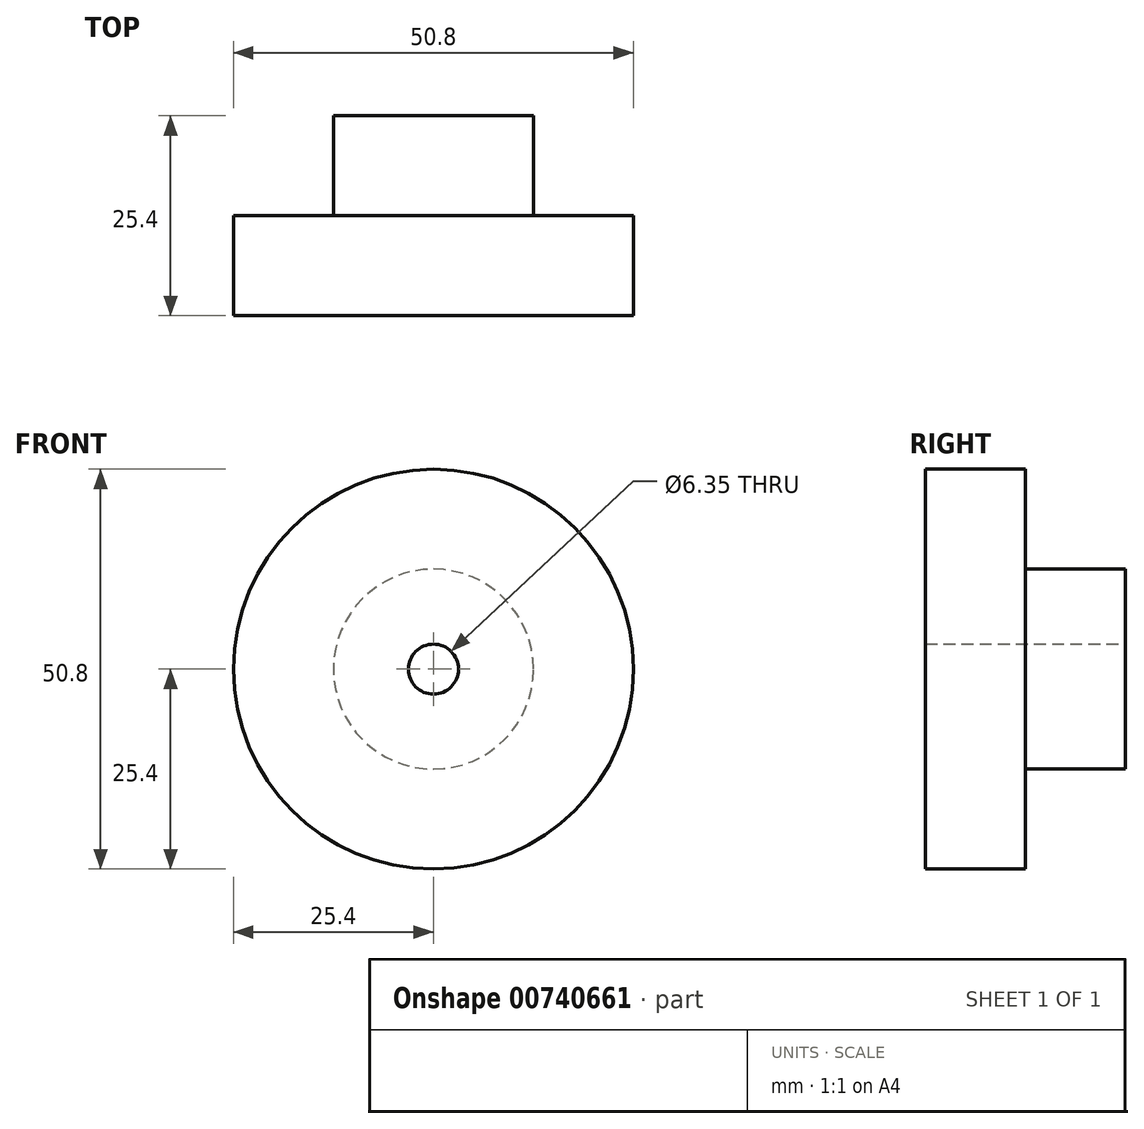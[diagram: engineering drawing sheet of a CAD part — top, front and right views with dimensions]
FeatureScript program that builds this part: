
annotation { "Feature Type Name" : "Feature", "Feature Type Description" : "" }
export const myFeature = defineFeature(function(context is Context, id is Id, definition is map)
    precondition{}
    {
        {
            var Q0;
            Q0=qCreatedBy(makeId("Top.planeOp"),FACE);
            var sketch = newSketch(context, id + "F0", { "sketchPlane" : qUnion([Q0])});
            skLineSegment(sketch, "E0", {"start": v(0, 0) * mm, "end": v(-25.4, 0) * mm});
            skLineSegment(sketch, "E1", {"start": v(-25.4, 0) * mm, "end": v(-25.4, 12.7) * mm});
            skLineSegment(sketch, "E2", {"start": v(-25.4, 12.7) * mm, "end": v(-12.7, 12.7) * mm});
            skLineSegment(sketch, "E3", {"start": v(-12.7, 12.7) * mm, "end": v(-12.7, 25.4) * mm});
            skLineSegment(sketch, "E4", {"start": v(-12.7, 25.4) * mm, "end": v(0, 25.4) * mm});
            skLineSegment(sketch, "E5", {"start": v(0, 25.4) * mm, "end": v(0, 0) * mm});
            skSolve(sketch);
        }
        {
            var Q0;
            Q0 = qSketchRegion(id + "F0", true);
            var Q1;
            Q1=sQuery(id+"F0.wireOp",EDGE,"E5");
            revolve(context, id + "F1", {"surfaceOperationType" : NewSurfaceOperationType.NEW, "entities" : qUnion([Q0]), "axis" : qUnion([Q1]), "revolveType" : RevolveType.FULL});
        }
        {
            var Q0;
            Q0=makeQuery(id+"F1.opRevolve","SWEPT_FACE",FACE,{"disambiguationData":[OSD([sQuery(id+"F0.wireOp",EDGE,"E4")])]});
            var sketch = newSketch(context, id + "F2", { "sketchPlane" : qUnion([Q0])});
            skPoint(sketch, "E6", {"position": v(0, 0) * mm});
            skCircle(sketch, "E7", {"center": v(0, 0) * mm, "radius": 3.81 * mm});
            skSolve(sketch);
        }
        {
            var Q0;
            Q0=sQuery(id+"F2.wireOp",VERTEX,"E6");
            var Q1;
            Q1=makeQuery(id+"F1.opRevolve","SWEPT_BODY",BODY,{"disambiguationData":[OSD([sQuery(id+"F0.wireOp",EDGE,"E0"),sQuery(id+"F0.wireOp",EDGE,"E1"),sQuery(id+"F0.wireOp",EDGE,"E2"),sQuery(id+"F0.wireOp",EDGE,"E3"),sQuery(id+"F0.wireOp",EDGE,"E4"),sQuery(id+"F0.wireOp",EDGE,"E5")])]});
            hole(context, id + "F3", {"style" : HoleStyle.SIMPLE, "endStyle" : HoleEndStyle.THROUGH, "holeDiameter" : 6.35 * mm, "majorDiameter" : 6.35 * mm, "isTappedThrough" : true, "tappedDepth" : 12.7 * mm, "tapClearance" : 3, "locations" : qUnion([Q0]), "scope" : qUnion([Q1])});
        }
    });
